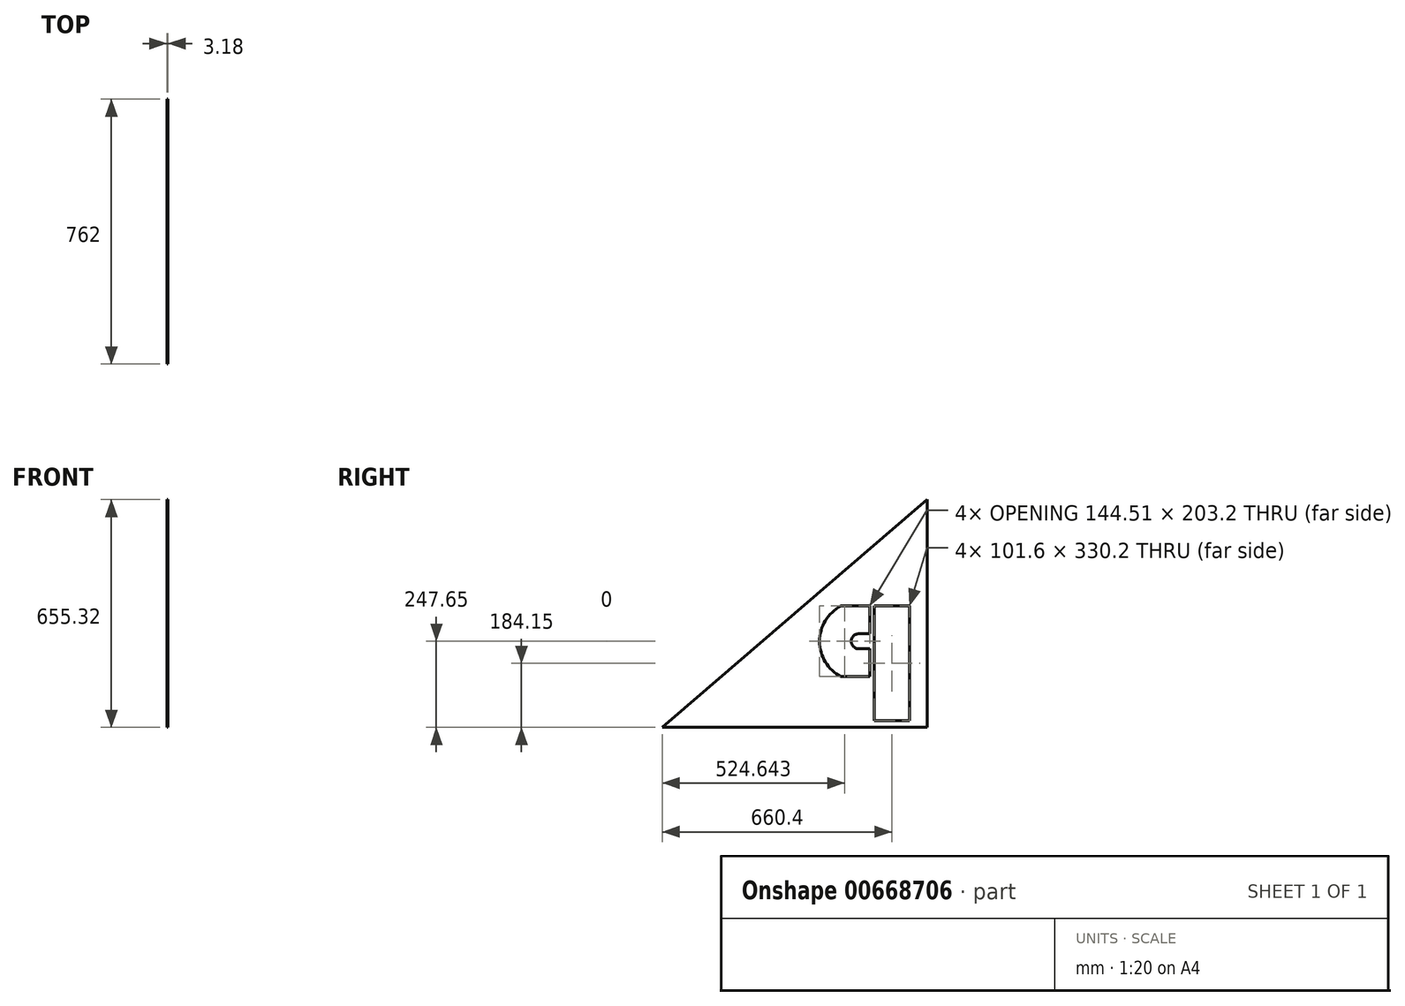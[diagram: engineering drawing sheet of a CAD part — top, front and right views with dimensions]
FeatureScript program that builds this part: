
annotation { "Feature Type Name" : "Feature", "Feature Type Description" : "" }
export const myFeature = defineFeature(function(context is Context, id is Id, definition is map)
    precondition{}
    {
        {
            var Q0;
            Q0=qCreatedBy(makeId("Right.planeOp"),FACE);
            var sketch = newSketch(context, id + "F0", { "sketchPlane" : qUnion([Q0])});
            skLineSegment(sketch, "E0.bottom", {"start": v(0, 0) * mm, "end": v(-762, 0) * mm});
            skLineSegment(sketch, "E0.left", {"start": v(0, 0) * mm, "end": v(0, 655.32) * mm});
            skLineSegment(sketch, "E1", {"start": v(0, 655.32) * mm, "end": v(-762, 0) * mm});
            skSolve(sketch);
        }
        {
            var Q0;
            Q0 = qSketchRegion(id + "F0", true);
            extrude(context, id + "F1", {"entities" : qUnion([Q0]), "depth" : 3.17 * mm, "offsetDistance" : 25.4 * mm});
        }
        {
            var Q0;
            Q0=makeQuery(id+"F1.opExtrude","CAP_FACE",FACE,{"disambiguationData":[OSD([sQuery(id+"F0.wireOp",EDGE,"E0.bottom"),sQuery(id+"F0.wireOp",EDGE,"E0.left"),sQuery(id+"F0.wireOp",EDGE,"E1")])],"isStart":true});
            var sketch = newSketch(context, id + "F2", { "sketchPlane" : qUnion([Q0])});
            skLineSegment(sketch, "E2.bottom", {"start": v(50.8, 19.05) * mm, "end": v(152.4, 19.05) * mm});
            skLineSegment(sketch, "E2.top", {"start": v(50.8, 349.25) * mm, "end": v(152.4, 349.25) * mm});
            skLineSegment(sketch, "E2.left", {"start": v(50.8, 19.05) * mm, "end": v(50.8, 349.25) * mm});
            skLineSegment(sketch, "E2.right", {"start": v(152.4, 19.05) * mm, "end": v(152.4, 349.25) * mm});
            skArc(sketch, "E3", {"start": v(247.65, 146.05) * mm, "mid": v(309.61, 247.65) * mm, "end": v(247.65, 349.25) * mm});
            skLineSegment(sketch, "E4.0", {"start": v(6.35, 641.48) * mm, "end": v(6.35, 6.35) * mm});
            skLineSegment(sketch, "E4.1", {"start": v(744.88, 6.35) * mm, "end": v(6.35, 641.48) * mm});
            skLineSegment(sketch, "E4.2", {"start": v(6.35, 6.35) * mm, "end": v(744.88, 6.35) * mm});
            skLineSegment(sketch, "E5", {"start": v(247.65, 349.25) * mm, "end": v(165.1, 349.25) * mm});
            skLineSegment(sketch, "E6", {"start": v(165.1, 349.25) * mm, "end": v(165.1, 269.24) * mm});
            skLineSegment(sketch, "E7", {"start": v(165.1, 226.06) * mm, "end": v(165.1, 146.05) * mm});
            skLineSegment(sketch, "E8", {"start": v(165.1, 146.05) * mm, "end": v(247.65, 146.05) * mm});
            skLineSegment(sketch, "E9", {"start": v(165.1, 226.06) * mm, "end": v(196.85, 226.06) * mm});
            skLineSegment(sketch, "E10", {"start": v(196.85, 269.24) * mm, "end": v(165.1, 269.24) * mm});
            skArc(sketch, "E11", {"start": v(196.85, 269.24) * mm, "mid": v(218.44, 247.65) * mm, "end": v(196.85, 226.06) * mm});
            skSolve(sketch);
        }
        {
            var Q0;
            Q0=makeQuery(id+"F2.imprint","IMPRINT",FACE,{"disambiguationData":[TD([[makeQuery(id+"F2.imprint","IMPRINT",EDGE,{"derivedFrom":sQuery(id+"F2.wireOp",EDGE,"E3")}),1.0]])]});
            var Q1;
            Q1=makeQuery(id+"F2.imprint","IMPRINT",FACE,{"disambiguationData":[TD([[makeQuery(id+"F2.imprint","IMPRINT",EDGE,{"derivedFrom":sQuery(id+"F2.wireOp",EDGE,"E2.bottom")}),1.0]])]});
            extrude(context, id + "F3", {"entities" : qUnion([Q0, Q1]), "operationType" : NewBodyOperationType.REMOVE, "oppositeDirection" : true, "depth" : 25.4 * mm, "offsetDistance" : 25.4 * mm});
        }
    });
